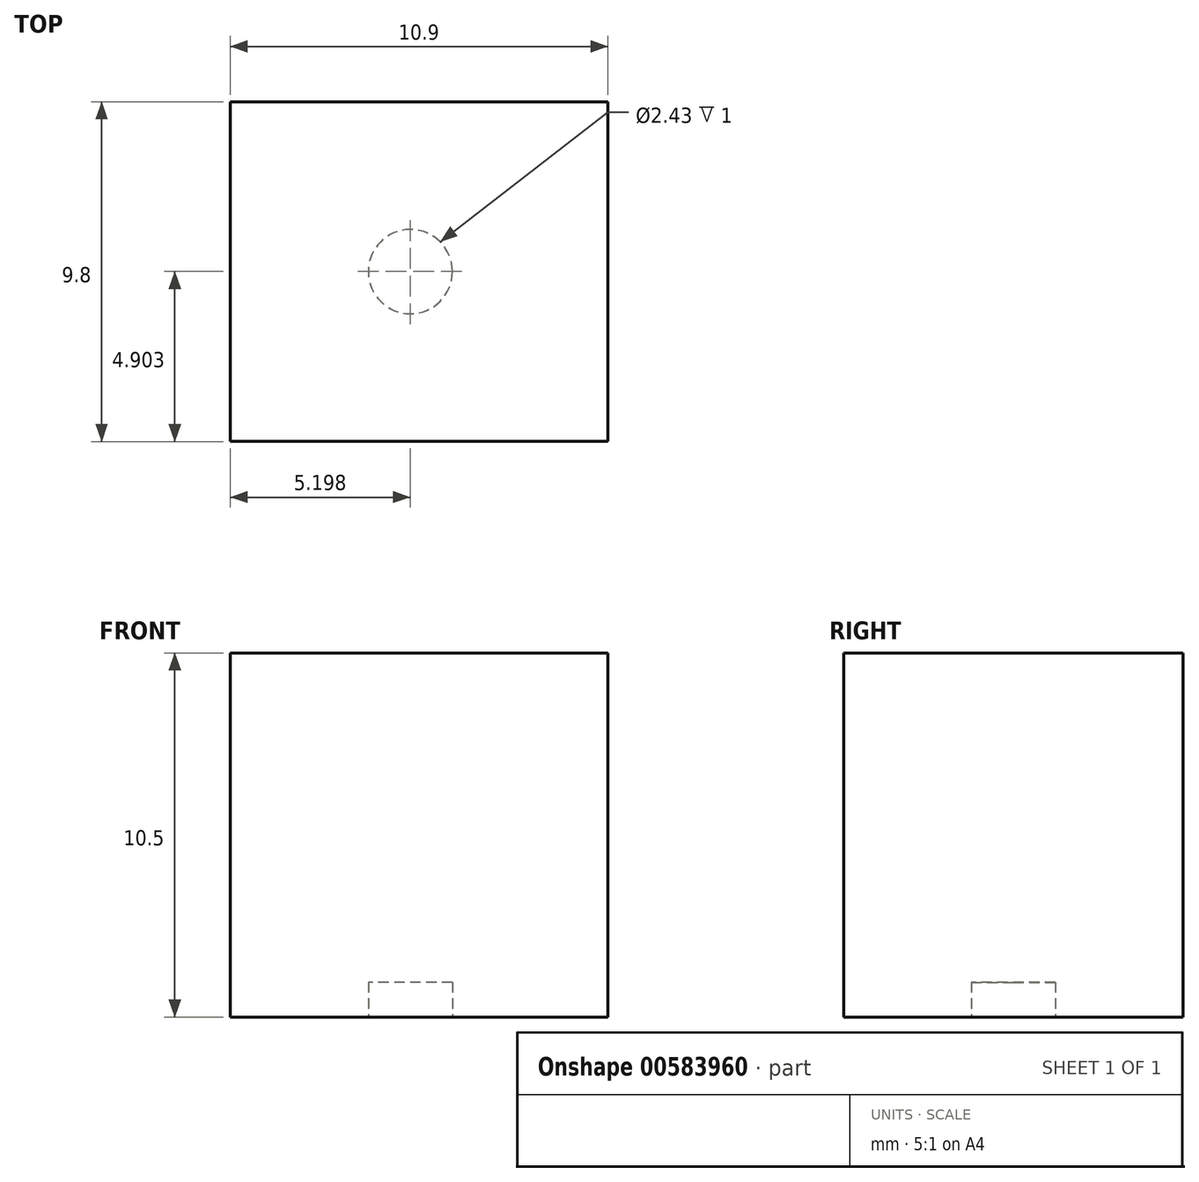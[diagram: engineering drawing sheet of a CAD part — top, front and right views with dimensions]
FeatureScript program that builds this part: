
annotation { "Feature Type Name" : "Feature", "Feature Type Description" : "" }
export const myFeature = defineFeature(function(context is Context, id is Id, definition is map)
    precondition{}
    {
        {
            var Q0;
            Q0=qCreatedBy(makeId("Top.planeOp"),FACE);
            var sketch = newSketch(context, id + "F0", { "sketchPlane" : qUnion([Q0])});
            skLineSegment(sketch, "E0.bottom", {"start": v(-2.56, 3.32) * mm, "end": v(8.34, 3.32) * mm});
            skLineSegment(sketch, "E0.top", {"start": v(-2.56, -6.48) * mm, "end": v(8.34, -6.48) * mm});
            skLineSegment(sketch, "E0.left", {"start": v(-2.56, 3.32) * mm, "end": v(-2.56, -6.48) * mm});
            skLineSegment(sketch, "E0.right", {"start": v(8.34, 3.32) * mm, "end": v(8.34, -6.48) * mm});
            skLineSegment(sketch, "E1", {"start": v(2.89, 3.32) * mm, "end": v(2.89, -6.48) * mm, "construction": true});
            skLineSegment(sketch, "E2", {"start": v(-2.56, -1.58) * mm, "end": v(8.34, -1.58) * mm, "construction": true});
            skPoint(sketch, "E3", {"position": v(2.89, -1.58) * mm});
            skSolve(sketch);
        }
        {
            var Q0;
            Q0 = qSketchRegion(id + "F0", true);
            extrude(context, id + "F1", {"entities" : qUnion([Q0]), "depth" : 10.5 * mm, "offsetDistance" : 25.4 * mm});
        }
        {
            var Q0;
            Q0=makeQuery(id+"F0.imprint","IMPRINT",FACE,{"disambiguationData":[TD([[makeQuery(id+"F0.imprint","IMPRINT",EDGE,{"derivedFrom":sQuery(id+"F0.wireOp",EDGE,"E0.bottom")}),-1.0]])]});
            var sketch = newSketch(context, id + "F2", { "sketchPlane" : qUnion([Q0])});
            skPoint(sketch, "E4.0", {"position": v(2.64, -1.58) * mm});
            skLineSegment(sketch, "E5.0", {"start": v(-2.56, 3.32) * mm, "end": v(8.34, 3.32) * mm, "construction": true});
            skLineSegment(sketch, "E6.0", {"start": v(-2.56, 3.32) * mm, "end": v(-2.56, -6.48) * mm, "construction": true});
            skCircle(sketch, "E7", {"center": v(2.64, -1.58) * mm, "radius": 1.21 * mm});
            skSolve(sketch);
        }
        {
            var Q0;
            Q0 = qSketchRegion(id + "F2", true);
            extrude(context, id + "F3", {"entities" : qUnion([Q0]), "operationType" : NewBodyOperationType.REMOVE, "depth" : 1 * mm, "offsetDistance" : 25.4 * mm});
        }
    });
